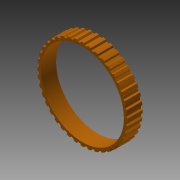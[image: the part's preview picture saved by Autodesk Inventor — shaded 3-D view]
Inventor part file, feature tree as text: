
AUTODESK INVENTOR PART (.ipt)
format: ipt  version: 2013 (Build 170138000, 138)  size: 273,408 bytes
history: native  units: in
note: dims shown in document units (in); Inventor stores cm internally (conversion verified against a paired STEP export)
features: extrude x1, sketch x1
ambient origin geometry x8: Origin, YZ Plane, XZ Plane, XY Plane, X Axis, Y Axis, Z Axis, Center Point
bodies: Solid1 (feature_tree)
feature tree (2):
  extrude  "Extrusion1"  Depth=5.6in
  sketch  "Sketch1"  dims[d0=1.02in d1=0.0in d2=5.6in]
